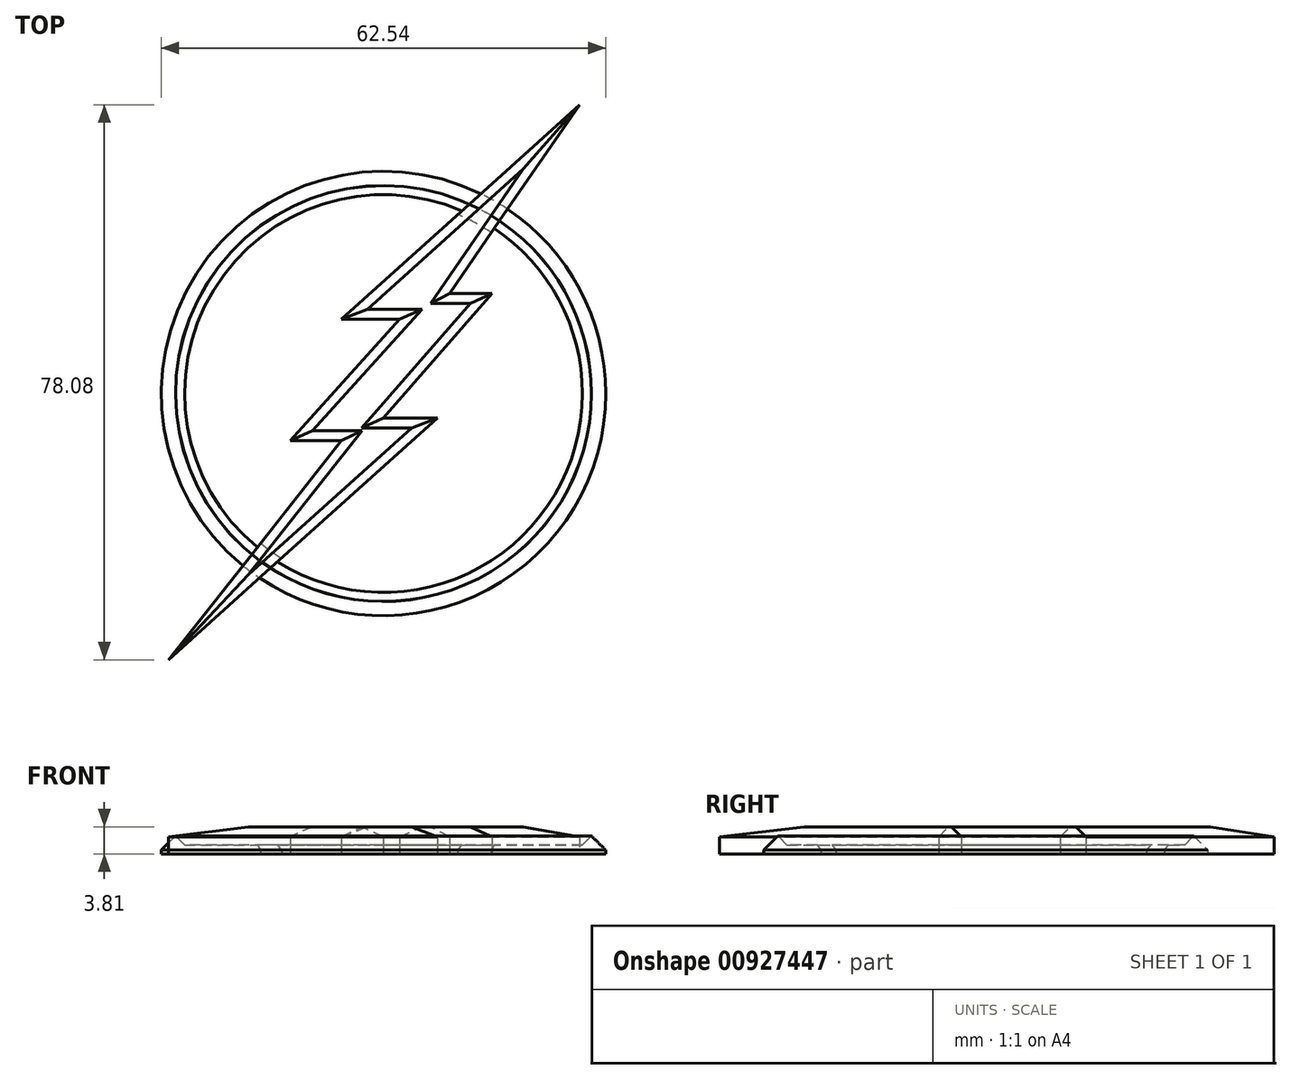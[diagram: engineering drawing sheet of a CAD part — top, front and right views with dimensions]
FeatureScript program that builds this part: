
annotation { "Feature Type Name" : "Feature", "Feature Type Description" : "" }
export const myFeature = defineFeature(function(context is Context, id is Id, definition is map)
    precondition{}
    {
        {
            var Q0;
            Q0=qCreatedBy(makeId("Top.planeOp"),FACE);
            var sketch = newSketch(context, id + "F0", { "sketchPlane" : qUnion([Q0])});
            skCircle(sketch, "E0", {"center": v(0, 0) * mm, "radius": 27.24 * mm});
            skCircle(sketch, "E1", {"center": v(0, 0) * mm, "radius": 31.27 * mm});
            skLineSegment(sketch, "E2", {"start": v(27.6, 40.6) * mm, "end": v(-5.9, 10.48) * mm});
            skLineSegment(sketch, "E3", {"start": v(-5.9, 10.48) * mm, "end": v(2.29, 10.48) * mm});
            skLineSegment(sketch, "E4", {"start": v(2.29, 10.48) * mm, "end": v(-13.13, -6.63) * mm});
            skLineSegment(sketch, "E5", {"start": v(-13.13, -6.63) * mm, "end": v(-5.9, -6.63) * mm});
            skLineSegment(sketch, "E6", {"start": v(-5.9, -6.63) * mm, "end": v(-30.24, -37.47) * mm});
            skLineSegment(sketch, "E7", {"start": v(-30.24, -37.47) * mm, "end": v(7.6, -3.43) * mm});
            skLineSegment(sketch, "E8", {"start": v(7.6, -3.43) * mm, "end": v(0, -3.43) * mm});
            skLineSegment(sketch, "E9", {"start": v(0, -3.43) * mm, "end": v(15.3, 14.1) * mm});
            skLineSegment(sketch, "E10", {"start": v(15.3, 14.1) * mm, "end": v(9.28, 14.1) * mm});
            skLineSegment(sketch, "E11", {"start": v(9.28, 14.1) * mm, "end": v(27.6, 40.6) * mm});
            skSolve(sketch);
        }
        {
            var Q0;
            {var subQ0=sQuery(id+"F0.wireOp",EDGE,"E2");var subQ1=sQuery(id+"F0.wireOp",EDGE,"E0");var subQ2=makeQuery(id+"F0.imprint","INTERSECT",VERTEX,{"derivedFrom":[subQ1,subQ0]});Q0=makeQuery(id+"F0.imprint","IMPRINT",FACE,{"disambiguationData":[TD([[makeQuery(id+"F0.imprint","IMPRINT",EDGE,{"disambiguationData":[TD([[subQ2,-1.0]])],"derivedFrom":subQ1}),-1.0]])]});}
            var Q1;
            {var subQ0=sQuery(id+"F0.wireOp",EDGE,"E11");var subQ1=sQuery(id+"F0.wireOp",EDGE,"E0");var subQ2=makeQuery(id+"F0.imprint","INTERSECT",VERTEX,{"derivedFrom":[subQ1,subQ0]});Q1=makeQuery(id+"F0.imprint","IMPRINT",FACE,{"disambiguationData":[TD([[makeQuery(id+"F0.imprint","IMPRINT",EDGE,{"disambiguationData":[TD([[subQ2,1.0]])],"derivedFrom":subQ1}),-1.0]])]});}
            var Q2;
            {var subQ0=sQuery(id+"F0.wireOp",EDGE,"E6");var subQ1=sQuery(id+"F0.wireOp",EDGE,"E0");var subQ2=makeQuery(id+"F0.imprint","INTERSECT",VERTEX,{"derivedFrom":[subQ1,subQ0]});Q2=makeQuery(id+"F0.imprint","IMPRINT",FACE,{"disambiguationData":[TD([[makeQuery(id+"F0.imprint","IMPRINT",EDGE,{"disambiguationData":[TD([[subQ2,-1.0]])],"derivedFrom":subQ1}),-1.0]])]});}
            var Q3;
            {var subQ0=sQuery(id+"F0.wireOp",EDGE,"E2");var subQ1=sQuery(id+"F0.wireOp",EDGE,"E0");var subQ2=makeQuery(id+"F0.imprint","INTERSECT",VERTEX,{"derivedFrom":[subQ1,subQ0]});Q3=makeQuery(id+"F0.imprint","IMPRINT",FACE,{"disambiguationData":[TD([[makeQuery(id+"F0.imprint","IMPRINT",EDGE,{"disambiguationData":[TD([[subQ2,1.0]])],"derivedFrom":subQ1}),-1.0]])]});}
            extrude(context, id + "F1", {"entities" : qUnion([Q0, Q1, Q2, Q3]), "depth" : 2.54 * mm, "offsetDistance" : 25.4 * mm});
        }
        {
            var Q0;
            {var subQ5=sQuery(id+"F0.wireOp",EDGE,"E3");Q0=makeQuery(id+"F0.imprint","IMPRINT",FACE,{"disambiguationData":[TD([[makeQuery(id+"F0.imprint","IMPRINT",EDGE,{"derivedFrom":subQ5}),-1.0]])]});}
            var Q1;
            {var subQ0=sQuery(id+"F0.wireOp",EDGE,"E8");Q1=makeQuery(id+"F0.imprint","IMPRINT",FACE,{"disambiguationData":[TD([[makeQuery(id+"F0.imprint","IMPRINT",EDGE,{"derivedFrom":subQ0}),-1.0]])]});}
            extrude(context, id + "F2", {"entities" : qUnion([Q0, Q1]), "operationType" : NewBodyOperationType.ADD, "depth" : 1.27 * mm, "offsetDistance" : 25.4 * mm});
        }
        {
            var Q0;
            {var subQ0=sQuery(id+"F0.wireOp",EDGE,"E6");var subQ1=sQuery(id+"F0.wireOp",EDGE,"E0");var subQ2=makeQuery(id+"F0.imprint","INTERSECT",VERTEX,{"derivedFrom":[subQ1,subQ0]});Q0=makeQuery(id+"F0.imprint","IMPRINT",FACE,{"disambiguationData":[TD([[makeQuery(id+"F0.imprint","IMPRINT",EDGE,{"disambiguationData":[TD([[subQ2,-1.0]])],"derivedFrom":subQ1}),-1.0]])]});}
            var Q1;
            {var subQ7=sQuery(id+"F0.wireOp",EDGE,"E3");Q1=makeQuery(id+"F0.imprint","IMPRINT",FACE,{"disambiguationData":[TD([[makeQuery(id+"F0.imprint","IMPRINT",EDGE,{"derivedFrom":subQ7}),1.0]])]});}
            var Q2;
            {var subQ0=sQuery(id+"F0.wireOp",EDGE,"E2");var subQ1=sQuery(id+"F0.wireOp",EDGE,"E0");var subQ2=makeQuery(id+"F0.imprint","INTERSECT",VERTEX,{"derivedFrom":[subQ1,subQ0]});Q2=makeQuery(id+"F0.imprint","IMPRINT",FACE,{"disambiguationData":[TD([[makeQuery(id+"F0.imprint","IMPRINT",EDGE,{"disambiguationData":[TD([[subQ2,1.0]])],"derivedFrom":subQ1}),-1.0]])]});}
            var Q3;
            {var subQ0=sQuery(id+"F0.wireOp",EDGE,"E2");var subQ1=sQuery(id+"F0.wireOp",EDGE,"E1");var subQ2=makeQuery(id+"F0.imprint","INTERSECT",VERTEX,{"derivedFrom":[subQ1,subQ0]});Q3=makeQuery(id+"F0.imprint","IMPRINT",FACE,{"disambiguationData":[TD([[makeQuery(id+"F0.imprint","IMPRINT",EDGE,{"disambiguationData":[TD([[subQ2,1.0]])],"derivedFrom":subQ1}),-1.0]])]});}
            var Q4;
            {var subQ0=sQuery(id+"F0.wireOp",EDGE,"E6");var subQ1=sQuery(id+"F0.wireOp",EDGE,"E1");var subQ2=makeQuery(id+"F0.imprint","INTERSECT",VERTEX,{"derivedFrom":[subQ1,subQ0]});Q4=makeQuery(id+"F0.imprint","IMPRINT",FACE,{"disambiguationData":[TD([[makeQuery(id+"F0.imprint","IMPRINT",EDGE,{"disambiguationData":[TD([[subQ2,-1.0]])],"derivedFrom":subQ1}),-1.0]])]});}
            extrude(context, id + "F3", {"entities" : qUnion([Q0, Q1, Q2, Q3, Q4]), "depth" : 3.8 * mm, "offsetDistance" : 25.4 * mm});
        }
        {
            var Q0;
            Q0=makeQuery(id+"F3.opExtrude","CAP_FACE",FACE,{"disambiguationData":[OSD([sQuery(id+"F0.wireOp",EDGE,"E2"),sQuery(id+"F0.wireOp",EDGE,"E3"),sQuery(id+"F0.wireOp",EDGE,"E4"),sQuery(id+"F0.wireOp",EDGE,"E5"),sQuery(id+"F0.wireOp",EDGE,"E6"),sQuery(id+"F0.wireOp",EDGE,"E7"),sQuery(id+"F0.wireOp",EDGE,"E8"),sQuery(id+"F0.wireOp",EDGE,"E9"),sQuery(id+"F0.wireOp",EDGE,"E10"),sQuery(id+"F0.wireOp",EDGE,"E11")])],"isStart":false});
            chamfer(context, id + "F4", {"entities" : qUnion([Q0]), "width" : 1.4 * mm, "tangentPropagation" : true});
        }
        {
            var Q0;
            Q0=makeQuery(id+"F1.opExtrude","CAP_FACE",FACE,{"disambiguationData":[OSD([sQuery(id+"F0.wireOp",EDGE,"E0"),sQuery(id+"F0.wireOp",EDGE,"E1")])],"isStart":false});
            chamfer(context, id + "F5", {"entities" : qUnion([Q0]), "width" : 2 * mm, "tangentPropagation" : true});
        }
    });
